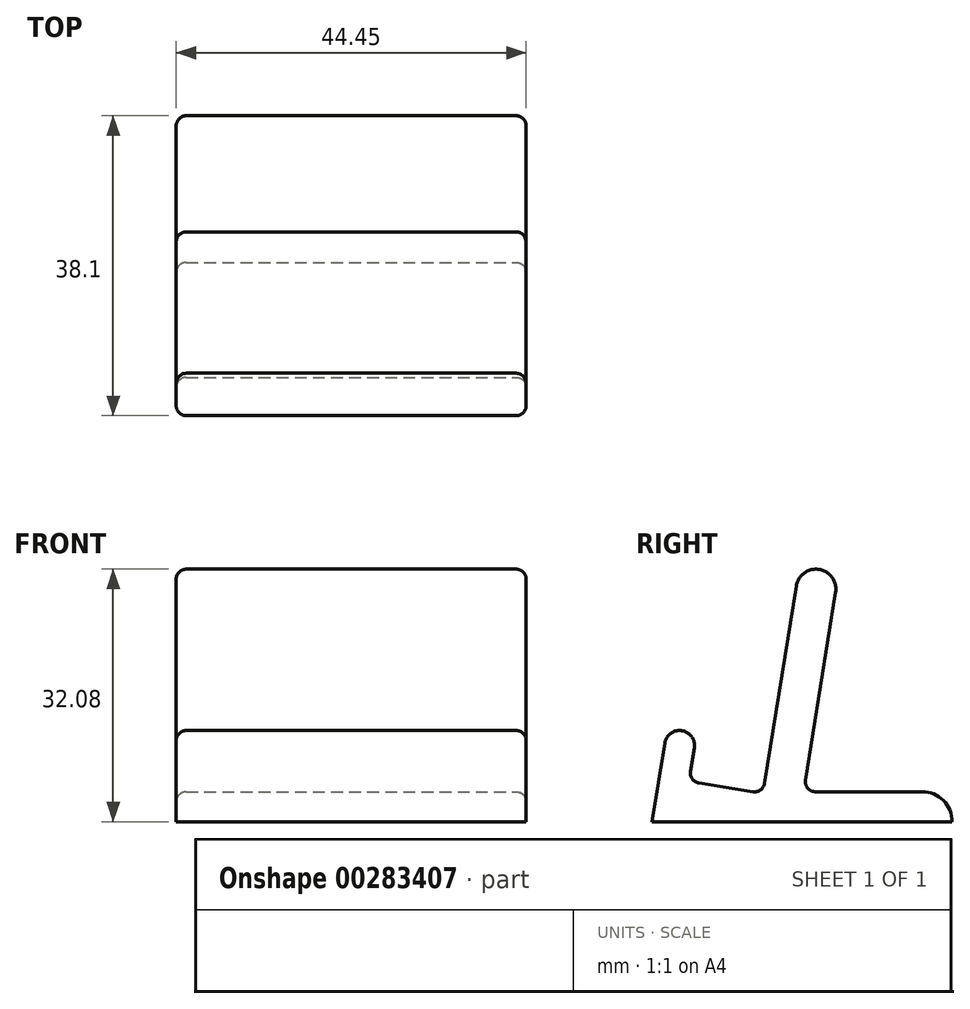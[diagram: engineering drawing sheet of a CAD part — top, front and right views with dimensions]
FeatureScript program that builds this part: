
annotation { "Feature Type Name" : "Feature", "Feature Type Description" : "" }
export const myFeature = defineFeature(function(context is Context, id is Id, definition is map)
    precondition{}
    {
        {
            var Q0;
            Q0=qCreatedBy(makeId("Right.planeOp"),FACE);
            var sketch = newSketch(context, id + "F0", { "sketchPlane" : qUnion([Q0])});
            skLineSegment(sketch, "E0", {"start": v(0, 0) * mm, "end": v(-38.1, 0) * mm});
            skLineSegment(sketch, "E1", {"start": v(-38.1, 0) * mm, "end": v(-36.5, 9.99) * mm});
            skLineSegment(sketch, "E2", {"start": v(-32.73, 9.38) * mm, "end": v(-33.21, 6.39) * mm});
            skLineSegment(sketch, "E3", {"start": v(-32.15, 4.91) * mm, "end": v(-25.28, 3.8) * mm});
            skLineSegment(sketch, "E4", {"start": v(-23.8, 4.88) * mm, "end": v(-19.78, 29.95) * mm});
            skArc(sketch, "E5", {"start": v(-14.78, 29.15) * mm, "mid": v(-16.88, 32.05) * mm, "end": v(-19.78, 29.95) * mm});
            skArc(sketch, "E6", {"start": v(0, 0) * mm, "mid": v(-1.12, 2.7) * mm, "end": v(-3.81, 3.81) * mm});
            skArc(sketch, "E7", {"start": v(-32.73, 9.38) * mm, "mid": v(-34.31, 11.57) * mm, "end": v(-36.5, 9.99) * mm});
            skLineSegment(sketch, "E8", {"start": v(-25.28, 3.81) * mm, "end": v(0, 161.05) * mm, "construction": true});
            skLineSegment(sketch, "E9", {"start": v(0, 161.05) * mm, "end": v(0, 0) * mm, "construction": true});
            skLineSegment(sketch, "E10", {"start": v(-36.5, 9.99) * mm, "end": v(-36.2, 11.87) * mm, "construction": true});
            skLineSegment(sketch, "E11", {"start": v(-36.2, 11.87) * mm, "end": v(-32.43, 11.26) * mm, "construction": true});
            skLineSegment(sketch, "E12", {"start": v(-32.43, 11.26) * mm, "end": v(-32.73, 9.38) * mm, "construction": true});
            skLineSegment(sketch, "E13", {"start": v(-18.62, 5.28) * mm, "end": v(-14.78, 29.15) * mm});
            skArc(sketch, "E14", {"start": v(-33.21, 6.39) * mm, "mid": v(-32.99, 5.43) * mm, "end": v(-32.15, 4.91) * mm});
            skArc(sketch, "E15", {"start": v(-25.28, 3.81) * mm, "mid": v(-24.33, 4.04) * mm, "end": v(-23.8, 4.88) * mm});
            skLineSegment(sketch, "E16", {"start": v(-3.81, 3.81) * mm, "end": v(-17.36, 3.8) * mm});
            skArc(sketch, "E17", {"start": v(-18.62, 5.28) * mm, "mid": v(-18.33, 4.26) * mm, "end": v(-17.36, 3.81) * mm});
            skSolve(sketch);
        }
        {
            var Q0;
            Q0=makeQuery(id+"F0.imprint","IMPRINT",FACE,{"disambiguationData":[TD([[makeQuery(id+"F0.imprint","IMPRINT",EDGE,{"derivedFrom":sQuery(id+"F0.wireOp",EDGE,"E0")}),-1.0]])]});
            extrude(context, id + "F1", {"entities" : qUnion([Q0]), "oppositeDirection" : true, "depth" : 44.45 * mm});
        }
        {
            var Q0;
            Q0=makeQuery(id+"F1.opExtrude","CAP_EDGE",EDGE,{"disambiguationData":[OSD([sQuery(id+"F0.wireOp",EDGE,"E4")])],"isStart":true});
            var Q1;
            Q1=makeQuery(id+"F1.opExtrude","CAP_EDGE",EDGE,{"disambiguationData":[OSD([sQuery(id+"F0.wireOp",EDGE,"E4")])],"isStart":false});
            fillet(context, id + "F2", {"entities" : qUnion([Q0, Q1]), "radius" : 1.27 * mm, "tangentPropagation" : true, "allowEdgeOverflow" : false});
        }
    });
